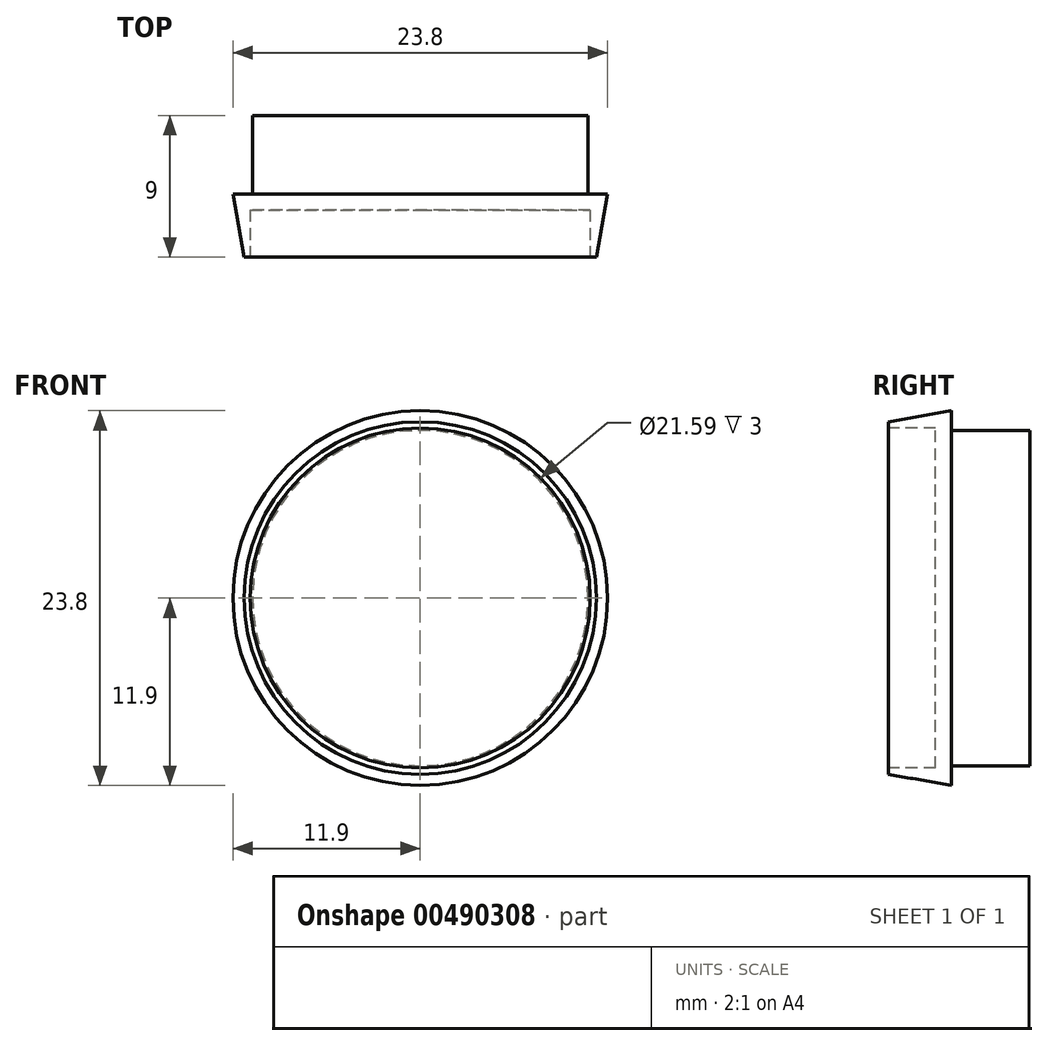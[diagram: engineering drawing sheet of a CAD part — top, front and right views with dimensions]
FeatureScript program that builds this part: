
annotation { "Feature Type Name" : "Feature", "Feature Type Description" : "" }
export const myFeature = defineFeature(function(context is Context, id is Id, definition is map)
    precondition{}
    {
        {
            var Q0;
            Q0=qCreatedBy(makeId("Front.planeOp"),FACE);
            var sketch = newSketch(context, id + "F0", { "sketchPlane" : qUnion([Q0])});
            skCircle(sketch, "E0", {"center": v(0, 0) * mm, "radius": 10.65 * mm});
            skCircle(sketch, "E1", {"center": v(0, 0) * mm, "radius": 11.9 * mm});
            skSolve(sketch);
        }
        {
            var Q0;
            Q0=makeQuery(id+"F0.imprint","IMPRINT",FACE,{"disambiguationData":[TD([[makeQuery(id+"F0.imprint","IMPRINT",EDGE,{"derivedFrom":sQuery(id+"F0.wireOp",EDGE,"E0")}),1.0]])]});
            extrude(context, id + "F1", {"entities" : qUnion([Q0]), "oppositeDirection" : true, "depth" : 5 * mm});
        }
        {
            var Q0;
            Q0=makeQuery(id+"F0.imprint","IMPRINT",FACE,{"disambiguationData":[TD([[makeQuery(id+"F0.imprint","IMPRINT",EDGE,{"derivedFrom":sQuery(id+"F0.wireOp",EDGE,"E0")}),1.0]])]});
            var Q1;
            Q1=makeQuery(id+"F0.imprint","IMPRINT",FACE,{"disambiguationData":[TD([[makeQuery(id+"F0.imprint","IMPRINT",EDGE,{"derivedFrom":sQuery(id+"F0.wireOp",EDGE,"E0")}),-1.0]])]});
            extrude(context, id + "F2", {"entities" : qUnion([Q0, Q1]), "operationType" : NewBodyOperationType.ADD, "depth" : 4 * mm, "hasDraft" : true, "draftAngle" : 10 * degree, "draftPullDirection" : true});
        }
        {
            var Q0;
            Q0=makeQuery(id+"F2.opExtrude","CAP_FACE",FACE,{"disambiguationData":[OSD([sQuery(id+"F0.wireOp",EDGE,"E1")])],"isStart":false});
            var sketch = newSketch(context, id + "F3", { "sketchPlane" : qUnion([Q0])});
            skCircle(sketch, "E2", {"center": v(0, 0) * mm, "radius": 10.8 * mm});
            skSolve(sketch);
        }
        {
            var Q0;
            Q0=makeQuery(id+"F3.imprint","IMPRINT",FACE,{"disambiguationData":[TD([[makeQuery(id+"F3.imprint","IMPRINT",EDGE,{"derivedFrom":sQuery(id+"F3.wireOp",EDGE,"E2")}),1.0]])]});
            extrude(context, id + "F4", {"entities" : qUnion([Q0]), "operationType" : NewBodyOperationType.REMOVE, "oppositeDirection" : true, "depth" : 3 * mm});
        }
    });
